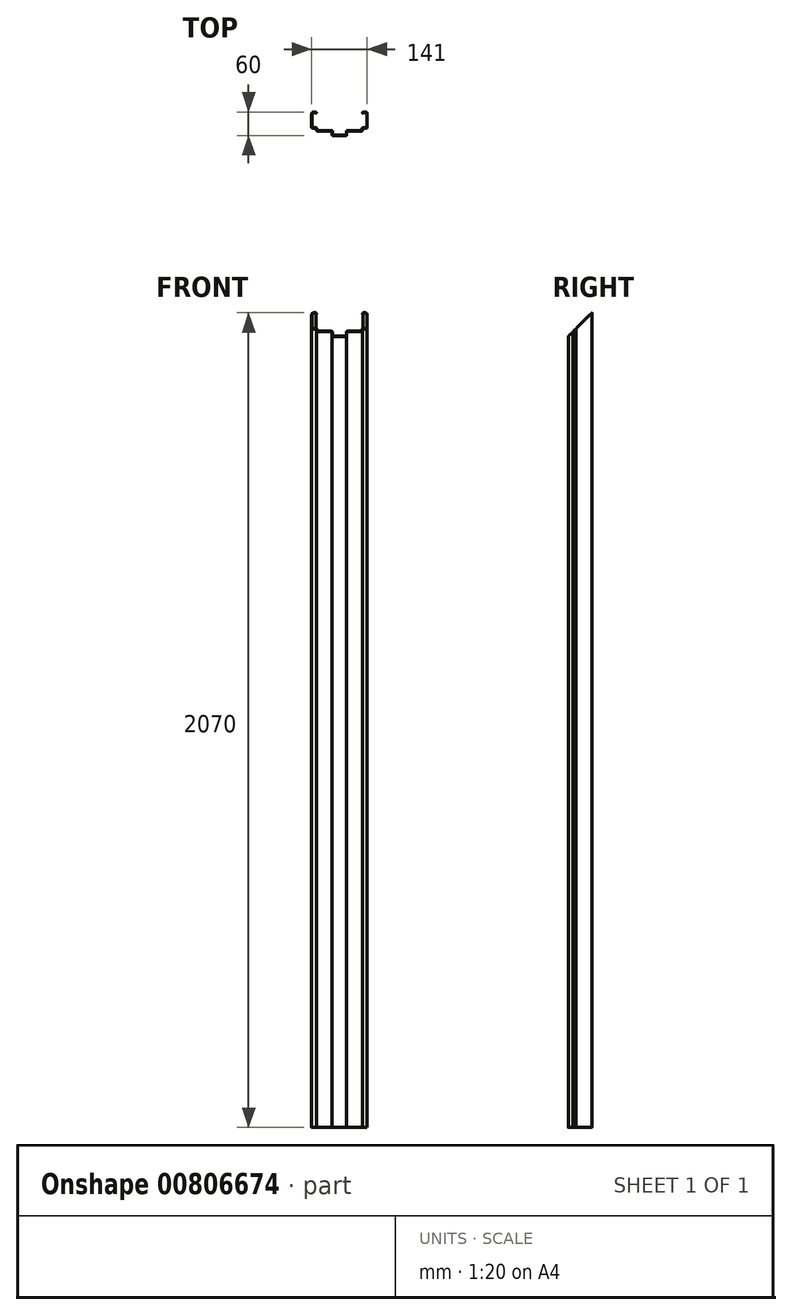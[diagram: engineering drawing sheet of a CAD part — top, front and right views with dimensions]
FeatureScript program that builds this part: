
annotation { "Feature Type Name" : "Feature", "Feature Type Description" : "" }
export const myFeature = defineFeature(function(context is Context, id is Id, definition is map)
    precondition{}
    {
        {
            var Q0;
            Q0=qCreatedBy(makeId("Top.planeOp"),FACE);
            var sketch = newSketch(context, id + "F0", { "sketchPlane" : qUnion([Q0])});
            skLineSegment(sketch, "E0", {"start": v(0, 0) * mm, "end": v(-18.5, 0) * mm});
            skLineSegment(sketch, "E1", {"start": v(-18.5, 0) * mm, "end": v(-18.5, 12) * mm});
            skLineSegment(sketch, "E2", {"start": v(-18.5, 12) * mm, "end": v(-58.5, 12) * mm});
            skLineSegment(sketch, "E3", {"start": v(-58.5, 12) * mm, "end": v(-58.5, 19) * mm});
            skLineSegment(sketch, "E4", {"start": v(-58.5, 19) * mm, "end": v(-70.5, 19) * mm});
            skLineSegment(sketch, "E5", {"start": v(-70.5, 19) * mm, "end": v(-70.5, 60) * mm});
            skLineSegment(sketch, "E6", {"start": v(-70.5, 60) * mm, "end": v(-58.5, 60) * mm});
            skLineSegment(sketch, "E7.MirrorCS", {"start": v(0, 0) * mm, "end": v(18.5, 0) * mm});
            skLineSegment(sketch, "E8.MirrorCS", {"start": v(18.5, 0) * mm, "end": v(18.5, 12) * mm});
            skLineSegment(sketch, "E9.MirrorCS", {"start": v(18.5, 12) * mm, "end": v(58.5, 12) * mm});
            skLineSegment(sketch, "E10.MirrorCS", {"start": v(58.5, 12) * mm, "end": v(58.5, 19) * mm});
            skLineSegment(sketch, "E11.MirrorCS", {"start": v(58.5, 19) * mm, "end": v(70.5, 19) * mm});
            skLineSegment(sketch, "E12.MirrorCS", {"start": v(70.5, 19) * mm, "end": v(70.5, 60) * mm});
            skLineSegment(sketch, "E13.MirrorCS", {"start": v(70.5, 60) * mm, "end": v(58.5, 60) * mm});
            skLineSegment(sketch, "E14", {"start": v(-58.5, 60) * mm, "end": v(-58.5, 57) * mm});
            skLineSegment(sketch, "E15.MirrorCS", {"start": v(58.5, 60) * mm, "end": v(58.5, 57) * mm});
            skLineSegment(sketch, "E16.0", {"start": v(-69.5, 20) * mm, "end": v(-69.5, 59) * mm});
            skLineSegment(sketch, "E16.1", {"start": v(-57.5, 20) * mm, "end": v(-69.5, 20) * mm});
            skLineSegment(sketch, "E16.2", {"start": v(0, 1) * mm, "end": v(-17.5, 1) * mm});
            skLineSegment(sketch, "E16.3", {"start": v(-17.5, 1) * mm, "end": v(-17.5, 13) * mm});
            skLineSegment(sketch, "E16.4", {"start": v(-17.5, 13) * mm, "end": v(-57.5, 13) * mm});
            skLineSegment(sketch, "E16.5", {"start": v(-57.5, 13) * mm, "end": v(-57.5, 20) * mm});
            skLineSegment(sketch, "E17", {"start": v(-69.5, 59) * mm, "end": v(-59.5, 59) * mm});
            skLineSegment(sketch, "E18", {"start": v(-59.5, 59) * mm, "end": v(-59.5, 57) * mm});
            skLineSegment(sketch, "E19", {"start": v(-59.5, 57) * mm, "end": v(-58.5, 57) * mm});
            skLineSegment(sketch, "E20.MirrorCS", {"start": v(0, 1) * mm, "end": v(17.5, 1) * mm});
            skLineSegment(sketch, "E21.MirrorCS", {"start": v(17.5, 1) * mm, "end": v(17.5, 13) * mm});
            skLineSegment(sketch, "E22.MirrorCS", {"start": v(17.5, 13) * mm, "end": v(57.5, 13) * mm});
            skLineSegment(sketch, "E23.MirrorCS", {"start": v(57.5, 13) * mm, "end": v(57.5, 20) * mm});
            skLineSegment(sketch, "E24.MirrorCS", {"start": v(57.5, 20) * mm, "end": v(69.5, 20) * mm});
            skLineSegment(sketch, "E25.MirrorCS", {"start": v(69.5, 20) * mm, "end": v(69.5, 59) * mm});
            skLineSegment(sketch, "E26.MirrorCS", {"start": v(69.5, 59) * mm, "end": v(59.5, 59) * mm});
            skLineSegment(sketch, "E27.MirrorCS", {"start": v(59.5, 59) * mm, "end": v(59.5, 57) * mm});
            skLineSegment(sketch, "E28.MirrorCS", {"start": v(59.5, 57) * mm, "end": v(58.5, 57) * mm});
            skSolve(sketch);
        }
        {
            var Q0;
            Q0=makeQuery(id+"F0.imprint","IMPRINT",FACE,{"disambiguationData":[TD([[makeQuery(id+"F0.imprint","IMPRINT",EDGE,{"derivedFrom":sQuery(id+"F0.wireOp",EDGE,"E0")}),-1.0]])]});
            extrude(context, id + "F1", {"entities" : qUnion([Q0]), "depth" : 2070 * mm, "offsetDistance" : 25 * mm});
        }
        {
            var Q0;
            Q0=makeQuery(id+"F1.opExtrude","SWEPT_EDGE",EDGE,{"disambiguationData":[OSD([sQuery(id+"F0.wireOp",EDGE,"E24.MirrorCS"),sQuery(id+"F0.wireOp",EDGE,"E25.MirrorCS")])]});
            var Q1;
            Q1=makeQuery(id+"F1.opExtrude","SWEPT_EDGE",EDGE,{"disambiguationData":[OSD([sQuery(id+"F0.wireOp",EDGE,"E23.MirrorCS"),sQuery(id+"F0.wireOp",EDGE,"E24.MirrorCS")])]});
            var Q2;
            Q2=makeQuery(id+"F1.opExtrude","SWEPT_EDGE",EDGE,{"disambiguationData":[OSD([sQuery(id+"F0.wireOp",EDGE,"E22.MirrorCS"),sQuery(id+"F0.wireOp",EDGE,"E23.MirrorCS")])]});
            var Q3;
            Q3=makeQuery(id+"F1.opExtrude","SWEPT_EDGE",EDGE,{"disambiguationData":[OSD([sQuery(id+"F0.wireOp",EDGE,"E21.MirrorCS"),sQuery(id+"F0.wireOp",EDGE,"E22.MirrorCS")])]});
            var Q4;
            Q4=makeQuery(id+"F1.opExtrude","SWEPT_EDGE",EDGE,{"disambiguationData":[OSD([sQuery(id+"F0.wireOp",EDGE,"E20.MirrorCS"),sQuery(id+"F0.wireOp",EDGE,"E21.MirrorCS")])]});
            var Q5;
            Q5=makeQuery(id+"F1.opExtrude","SWEPT_EDGE",EDGE,{"disambiguationData":[OSD([sQuery(id+"F0.wireOp",EDGE,"E17"),sQuery(id+"F0.wireOp",EDGE,"E18")])]});
            var Q6;
            Q6=makeQuery(id+"F1.opExtrude","SWEPT_EDGE",EDGE,{"disambiguationData":[OSD([sQuery(id+"F0.wireOp",EDGE,"E16.3"),sQuery(id+"F0.wireOp",EDGE,"E16.4")])]});
            var Q7;
            Q7=makeQuery(id+"F1.opExtrude","SWEPT_EDGE",EDGE,{"disambiguationData":[OSD([sQuery(id+"F0.wireOp",EDGE,"E16.1"),sQuery(id+"F0.wireOp",EDGE,"E16.5")])]});
            var Q8;
            Q8=makeQuery(id+"F1.opExtrude","SWEPT_EDGE",EDGE,{"disambiguationData":[OSD([sQuery(id+"F0.wireOp",EDGE,"E6"),sQuery(id+"F0.wireOp",EDGE,"E14")])]});
            var Q9;
            Q9=makeQuery(id+"F1.opExtrude","SWEPT_EDGE",EDGE,{"disambiguationData":[OSD([sQuery(id+"F0.wireOp",EDGE,"E16.2"),sQuery(id+"F0.wireOp",EDGE,"E16.3")])]});
            var Q10;
            Q10=makeQuery(id+"F1.opExtrude","SWEPT_EDGE",EDGE,{"disambiguationData":[OSD([sQuery(id+"F0.wireOp",EDGE,"E16.4"),sQuery(id+"F0.wireOp",EDGE,"E16.5")])]});
            var Q11;
            Q11=makeQuery(id+"F1.opExtrude","SWEPT_EDGE",EDGE,{"disambiguationData":[OSD([sQuery(id+"F0.wireOp",EDGE,"E16.0"),sQuery(id+"F0.wireOp",EDGE,"E16.1")])]});
            var Q12;
            Q12=makeQuery(id+"F1.opExtrude","SWEPT_EDGE",EDGE,{"disambiguationData":[OSD([sQuery(id+"F0.wireOp",EDGE,"E26.MirrorCS"),sQuery(id+"F0.wireOp",EDGE,"E27.MirrorCS")])]});
            var Q13;
            Q13=makeQuery(id+"F1.opExtrude","SWEPT_EDGE",EDGE,{"disambiguationData":[OSD([sQuery(id+"F0.wireOp",EDGE,"E13.MirrorCS"),sQuery(id+"F0.wireOp",EDGE,"E15.MirrorCS")])]});
            var Q14;
            Q14=makeQuery(id+"F1.opExtrude","SWEPT_EDGE",EDGE,{"disambiguationData":[OSD([sQuery(id+"F0.wireOp",EDGE,"E11.MirrorCS"),sQuery(id+"F0.wireOp",EDGE,"E12.MirrorCS")])]});
            var Q15;
            Q15=makeQuery(id+"F1.opExtrude","SWEPT_EDGE",EDGE,{"disambiguationData":[OSD([sQuery(id+"F0.wireOp",EDGE,"E10.MirrorCS"),sQuery(id+"F0.wireOp",EDGE,"E11.MirrorCS")])]});
            var Q16;
            Q16=makeQuery(id+"F1.opExtrude","SWEPT_EDGE",EDGE,{"disambiguationData":[OSD([sQuery(id+"F0.wireOp",EDGE,"E9.MirrorCS"),sQuery(id+"F0.wireOp",EDGE,"E10.MirrorCS")])]});
            var Q17;
            Q17=makeQuery(id+"F1.opExtrude","SWEPT_EDGE",EDGE,{"disambiguationData":[OSD([sQuery(id+"F0.wireOp",EDGE,"E8.MirrorCS"),sQuery(id+"F0.wireOp",EDGE,"E9.MirrorCS")])]});
            var Q18;
            Q18=makeQuery(id+"F1.opExtrude","SWEPT_EDGE",EDGE,{"disambiguationData":[OSD([sQuery(id+"F0.wireOp",EDGE,"E7.MirrorCS"),sQuery(id+"F0.wireOp",EDGE,"E8.MirrorCS")])]});
            var Q19;
            Q19=makeQuery(id+"F1.opExtrude","SWEPT_EDGE",EDGE,{"disambiguationData":[OSD([sQuery(id+"F0.wireOp",EDGE,"E0"),sQuery(id+"F0.wireOp",EDGE,"E1")])]});
            var Q20;
            Q20=makeQuery(id+"F1.opExtrude","SWEPT_EDGE",EDGE,{"disambiguationData":[OSD([sQuery(id+"F0.wireOp",EDGE,"E1"),sQuery(id+"F0.wireOp",EDGE,"E2")])]});
            var Q21;
            Q21=makeQuery(id+"F1.opExtrude","SWEPT_EDGE",EDGE,{"disambiguationData":[OSD([sQuery(id+"F0.wireOp",EDGE,"E2"),sQuery(id+"F0.wireOp",EDGE,"E3")])]});
            var Q22;
            Q22=makeQuery(id+"F1.opExtrude","SWEPT_EDGE",EDGE,{"disambiguationData":[OSD([sQuery(id+"F0.wireOp",EDGE,"E3"),sQuery(id+"F0.wireOp",EDGE,"E4")])]});
            var Q23;
            Q23=makeQuery(id+"F1.opExtrude","SWEPT_EDGE",EDGE,{"disambiguationData":[OSD([sQuery(id+"F0.wireOp",EDGE,"E4"),sQuery(id+"F0.wireOp",EDGE,"E5")])]});
            fillet(context, id + "F2", {"entities" : qUnion([Q0, Q1, Q2, Q3, Q4, Q5, Q6, Q7, Q8, Q9, Q10, Q11, Q12, Q13, Q14, Q15, Q16, Q17, Q18, Q19, Q20, Q21, Q22, Q23]), "radius" : 3 * mm, "rho" : 0.5, "crossSection" : FilletCrossSection.CONIC, "allowEdgeOverflow" : false});
        }
        {
            var Q0;
            Q0=makeQuery(id+"F1.opExtrude","SWEPT_EDGE",EDGE,{"disambiguationData":[OSD([sQuery(id+"F0.wireOp",EDGE,"E5"),sQuery(id+"F0.wireOp",EDGE,"E6")])]});
            var Q1;
            Q1=makeQuery(id+"F1.opExtrude","SWEPT_EDGE",EDGE,{"disambiguationData":[OSD([sQuery(id+"F0.wireOp",EDGE,"E16.0"),sQuery(id+"F0.wireOp",EDGE,"E17")])]});
            var Q2;
            Q2=makeQuery(id+"F1.opExtrude","SWEPT_EDGE",EDGE,{"disambiguationData":[OSD([sQuery(id+"F0.wireOp",EDGE,"E12.MirrorCS"),sQuery(id+"F0.wireOp",EDGE,"E13.MirrorCS")])]});
            var Q3;
            Q3=makeQuery(id+"F1.opExtrude","SWEPT_EDGE",EDGE,{"disambiguationData":[OSD([sQuery(id+"F0.wireOp",EDGE,"E25.MirrorCS"),sQuery(id+"F0.wireOp",EDGE,"E26.MirrorCS")])]});
            fillet(context, id + "F3", {"entities" : qUnion([Q0, Q1, Q2, Q3]), "radius" : 5 * mm, "allowEdgeOverflow" : false});
        }
        {
            var Q0;
            Q0=makeQuery(id+"F1.opExtrude","SWEPT_FACE",FACE,{"disambiguationData":[OSD([sQuery(id+"F0.wireOp",EDGE,"E12.MirrorCS")])]});
            cPlane(context, id + "F4", {"entities" : qUnion([Q0]), "cplaneType" : CPlaneType.OFFSET, "offset" : 0 * mm, "width" : 150 * mm, "height" : 150 * mm});
        }
        {
            var Q0;
            Q0=qCreatedBy(id+"F4.planeOp",FACE);
            var sketch = newSketch(context, id + "F5", { "sketchPlane" : qUnion([Q0])});
            skLineSegment(sketch, "E29", {"start": v(60, 2025.63) * mm, "end": v(60, 2082.85) * mm, "construction": true});
            skLineSegment(sketch, "E30", {"start": v(60, 2070) * mm, "end": v(-13.6, 2070) * mm, "construction": true});
            skLineSegment(sketch, "E31", {"start": v(60, 2070) * mm, "end": v(-1.52, 2008.48) * mm, "construction": true});
            skLineSegment(sketch, "E32", {"start": v(60, 2070) * mm, "end": v(-11.1, 2070) * mm});
            skLineSegment(sketch, "E33", {"start": v(-11.1, 2070) * mm, "end": v(-1.52, 2008.48) * mm});
            skLineSegment(sketch, "E34", {"start": v(39.84, 2070) * mm, "end": v(39.84, 0) * mm, "construction": true});
            skLineSegment(sketch, "E35", {"start": v(39.84, 1035) * mm, "end": v(248.17, 1035) * mm, "construction": true});
            skLineSegment(sketch, "E36.MirrorCS", {"start": v(-11.1, 0) * mm, "end": v(-1.52, 61.52) * mm});
            skLineSegment(sketch, "E37.MirrorCS", {"start": v(60, 0) * mm, "end": v(-13.6, 0) * mm, "construction": true});
            skLineSegment(sketch, "E38.MirrorCS", {"start": v(60, 0) * mm, "end": v(-1.52, 61.52) * mm, "construction": true});
            skLineSegment(sketch, "E39", {"start": v(-1.52, 61.52) * mm, "end": v(60, 0) * mm});
            skLineSegment(sketch, "E40", {"start": v(-11.1, 0) * mm, "end": v(60, 0) * mm});
            skLineSegment(sketch, "E41", {"start": v(-1.52, 2008.48) * mm, "end": v(60, 2070) * mm});
            skSolve(sketch);
        }
        {
            var Q0;
            Q0=makeQuery(id+"F5.imprint","IMPRINT",FACE,{"disambiguationData":[TD([[makeQuery(id+"F5.imprint","IMPRINT",EDGE,{"derivedFrom":sQuery(id+"F5.wireOp",EDGE,"E32")}),1.0]])]});
            extrude(context, id + "F6", {"entities" : qUnion([Q0]), "operationType" : NewBodyOperationType.REMOVE, "oppositeDirection" : true, "depth" : 166 * mm, "offsetDistance" : 25 * mm});
        }
    });
